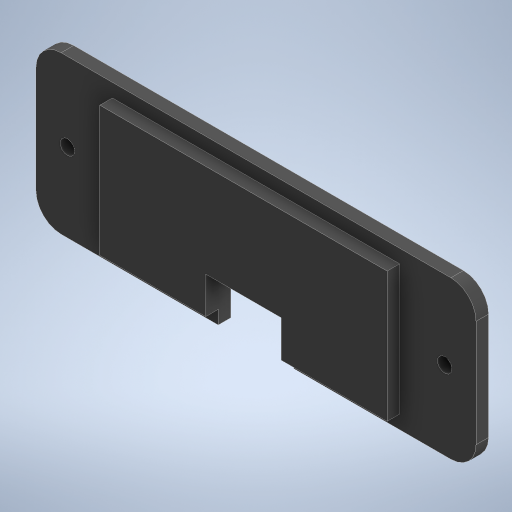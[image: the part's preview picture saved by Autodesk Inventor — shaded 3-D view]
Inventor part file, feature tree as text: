
AUTODESK INVENTOR PART (.ipt)
format: ipt  version: 2024.2 (Build 282272000, 272)  size: 278,016 bytes
history: native  units: mm
features: extrude x3, sketch x3, plane x1, fillet x1
ambient origin geometry x8: Origin, YZ Plane, XZ Plane, XY Plane, X Axis, Y Axis, Z Axis, Center Point
bodies: Solid1 (feature_tree)
feature tree (8):
  extrude  "Extrusion1"  Depth=25.0mm
  sketch  "Sketch4"  dims[d19=10.0mm d20=10.0mm]
  plane  "Work Plane1"
  sketch  "Sketch5"  dims[d21=2.3mm d22=2.3mm d25=20.7mm d26=2.15mm d27=45.7mm d32=12.0mm d33=8.0mm d36=4.0mm d37=12.5mm d38=12.5mm d39=12.5mm d40=5.0mm d41=5.0mm d42=12.5mm d43=12.5mm d44=12.15mm d45=2.0mm d46=0.0mm d50=29.0mm d51=0.0mm d52=0.0mm]
  fillet  "Fillet1"  Radius=2.0mm
  extrude  "Extrusion6"  Depth=10.0mm
  extrude  "Extrusion7"  Depth=29.0mm
  sketch  "Sketch1"  dims[d0=50.0mm d1=25.0mm d2=2.0mm d3=0.0mm]
